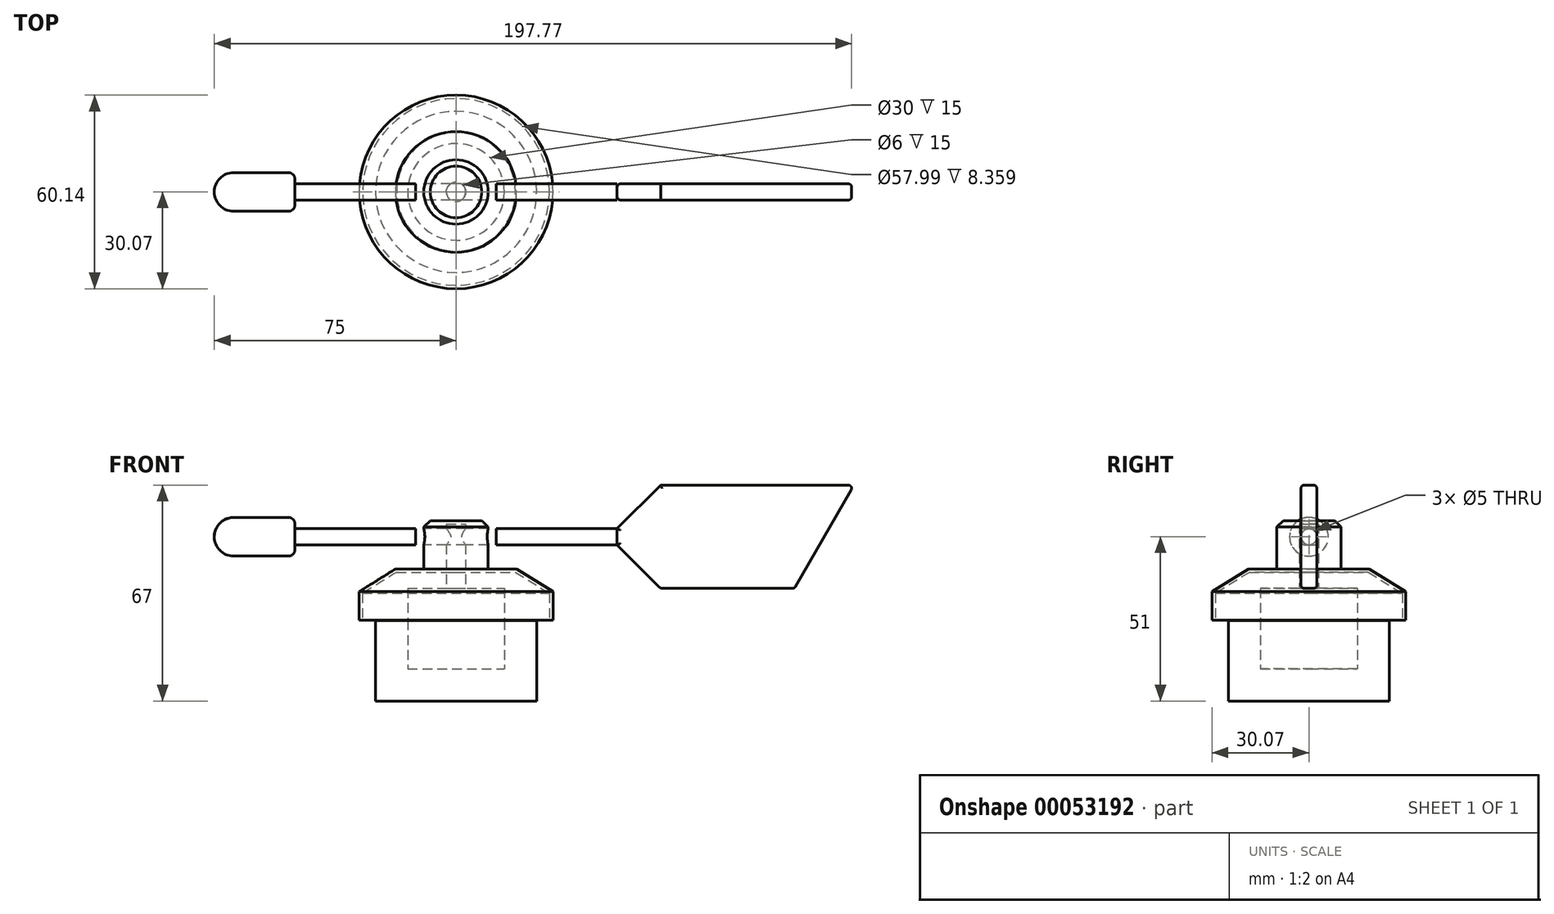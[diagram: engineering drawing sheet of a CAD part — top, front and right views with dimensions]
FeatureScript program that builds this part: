
annotation { "Feature Type Name" : "Feature", "Feature Type Description" : "" }
export const myFeature = defineFeature(function(context is Context, id is Id, definition is map)
    precondition{}
    {
        {
            var Q0;
            Q0=qCreatedBy(makeId("Front.planeOp"),FACE);
            var sketch = newSketch(context, id + "F0", { "sketchPlane" : qUnion([Q0])});
            skLineSegment(sketch, "E0", {"start": v(0, 0) * mm, "end": v(0, 20) * mm});
            skLineSegment(sketch, "E1", {"start": v(0, 20) * mm, "end": v(-3, 20) * mm});
            skLineSegment(sketch, "E2", {"start": v(-3, 20) * mm, "end": v(-3, 0) * mm});
            skLineSegment(sketch, "E3", {"start": v(-3, 0) * mm, "end": v(0, 0) * mm});
            skLineSegment(sketch, "E4", {"start": v(-3, 0) * mm, "end": v(-15, 0) * mm});
            skLineSegment(sketch, "E5", {"start": v(-15, 0) * mm, "end": v(-15, -25) * mm});
            skLineSegment(sketch, "E6", {"start": v(-15, -25) * mm, "end": v(0, -25) * mm});
            skLineSegment(sketch, "E7", {"start": v(0, -25) * mm, "end": v(0, 0) * mm});
            skLineSegment(sketch, "E8", {"start": v(-15, -10) * mm, "end": v(-25, -10) * mm});
            skLineSegment(sketch, "E9", {"start": v(-25, -10) * mm, "end": v(-25, -35) * mm});
            skLineSegment(sketch, "E10", {"start": v(-25, -35) * mm, "end": v(0, -35) * mm});
            skLineSegment(sketch, "E11", {"start": v(0, -35) * mm, "end": v(0, -25) * mm});
            skLineSegment(sketch, "E12", {"start": v(-10, 21) * mm, "end": v(-10, 6) * mm});
            skLineSegment(sketch, "E13", {"start": v(-10, 6) * mm, "end": v(-3, 6) * mm});
            skLineSegment(sketch, "E14", {"start": v(-10, 6) * mm, "end": v(-18.76, 6) * mm});
            skLineSegment(sketch, "E15", {"start": v(-18.76, 6) * mm, "end": v(-30.07, -1.04) * mm});
            skLineSegment(sketch, "E16", {"start": v(-30.07, -1.04) * mm, "end": v(-30.07, -9.93) * mm});
            skLineSegment(sketch, "E17", {"start": v(-30.07, -9.93) * mm, "end": v(-29, -9.93) * mm});
            skLineSegment(sketch, "E18", {"start": v(-29, -9.93) * mm, "end": v(-29, -1.58) * mm});
            skLineSegment(sketch, "E19", {"start": v(-29, -1.58) * mm, "end": v(-18.42, 5) * mm});
            skLineSegment(sketch, "E20", {"start": v(-18.42, 5) * mm, "end": v(-3, 5) * mm});
            skLineSegment(sketch, "E21", {"start": v(-10, 21) * mm, "end": v(0, 21) * mm});
            skLineSegment(sketch, "E22", {"start": v(0, 21) * mm, "end": v(0, 20) * mm});
            skSolve(sketch);
        }
        {
            var Q0;
            {var subQ2=sQuery(id+"F0.wireOp",EDGE,"E1");Q0=makeQuery(id+"F0.imprint","IMPRINT",FACE,{"disambiguationData":[TD([[makeQuery(id+"F0.imprint","IMPRINT",EDGE,{"derivedFrom":subQ2}),1.0]])]});}
            var Q1;
            Q1=sQuery(id+"F0.wireOp",EDGE,"E0");
            revolve(context, id + "F1", {"entities" : qUnion([Q0]), "axis" : qUnion([Q1]), "revolveType" : RevolveType.FULL});
        }
        {
            var Q0;
            Q0=makeQuery(id+"F0.imprint","IMPRINT",FACE,{"disambiguationData":[TD([[makeQuery(id+"F0.imprint","IMPRINT",EDGE,{"derivedFrom":sQuery(id+"F0.wireOp",EDGE,"E3")}),-1.0]])]});
            var Q1;
            Q1=sQuery(id+"F0.wireOp",EDGE,"E0");
            revolve(context, id + "F2", {"operationType" : NewBodyOperationType.ADD, "entities" : qUnion([Q0]), "axis" : qUnion([Q1]), "revolveType" : RevolveType.FULL});
        }
        {
            var Q0;
            {var subQ1=sQuery(id+"F0.wireOp",EDGE,"E6");Q0=makeQuery(id+"F0.imprint","IMPRINT",FACE,{"disambiguationData":[TD([[makeQuery(id+"F0.imprint","IMPRINT",EDGE,{"derivedFrom":subQ1}),-1.0]])]});}
            var Q1;
            Q1=sQuery(id+"F0.wireOp",EDGE,"E0");
            revolve(context, id + "F3", {"entities" : qUnion([Q0]), "axis" : qUnion([Q1]), "revolveType" : RevolveType.FULL});
        }
        {
            var Q0;
            {var subQ2=sQuery(id+"F0.wireOp",EDGE,"E1");Q0=makeQuery(id+"F0.imprint","IMPRINT",FACE,{"disambiguationData":[TD([[makeQuery(id+"F0.imprint","IMPRINT",EDGE,{"derivedFrom":subQ2}),-1.0]])]});}
            var Q1;
            {var subQ0=sQuery(id+"F0.wireOp",EDGE,"E13");Q1=makeQuery(id+"F0.imprint","IMPRINT",FACE,{"disambiguationData":[TD([[makeQuery(id+"F0.imprint","IMPRINT",EDGE,{"derivedFrom":subQ0}),-1.0]])]});}
            var Q2;
            Q2=sQuery(id+"F0.wireOp",EDGE,"E0");
            revolve(context, id + "F4", {"entities" : qUnion([Q0, Q1]), "axis" : qUnion([Q2]), "revolveType" : RevolveType.FULL});
        }
        {
            var Q0;
            Q0=qCreatedBy(makeId("Right.planeOp"),FACE);
            var sketch = newSketch(context, id + "F5", { "sketchPlane" : qUnion([Q0])});
            skCircle(sketch, "E23", {"center": v(0, 16) * mm, "radius": 2.5 * mm});
            skSolve(sketch);
        }
        {
            var Q0;
            Q0 = qSketchRegion(id + "F5", true);
            extrude(context, id + "F6", {"entities" : qUnion([Q0]), "endBound" : BoundingType.SYMMETRIC, "depth" : 100 * mm});
        }
        {
            var Q0;
            Q0=makeQuery(id+"F6.opExtrude","CAP_FACE",FACE,{"disambiguationData":[OSD([sQuery(id+"F5.wireOp",EDGE,"E23")])],"isStart":true});
            cPlane(context, id + "F7", {"entities" : qUnion([Q0]), "cplaneType" : CPlaneType.OFFSET, "offset" : 0 * mm, "width" : 150 * mm, "height" : 150 * mm});
        }
        {
            var Q0;
            Q0=qCreatedBy(id+"F7.planeOp",FACE);
            var sketch = newSketch(context, id + "F8", { "sketchPlane" : qUnion([Q0])});
            skCircle(sketch, "E24.0", {"center": v(0, 16) * mm, "radius": 2.5 * mm, "construction": true});
            skCircle(sketch, "E25", {"center": v(0, 16) * mm, "radius": 6 * mm});
            skSolve(sketch);
        }
        {
            var Q0;
            Q0=makeQuery(id+"F8.imprint","IMPRINT",FACE,{"disambiguationData":[TD([[makeQuery(id+"F8.imprint","IMPRINT",EDGE,{"derivedFrom":sQuery(id+"F8.wireOp",EDGE,"E25")}),1.0]])]});
            extrude(context, id + "F9", {"entities" : qUnion([Q0]), "depth" : 25 * mm});
        }
        {
            var Q0;
            Q0=makeQuery(id+"F9.opExtrude","CAP_EDGE",EDGE,{"disambiguationData":[OSD([sQuery(id+"F8.wireOp",EDGE,"E25")])],"isStart":false});
            fillet(context, id + "F10", {"entities" : qUnion([Q0]), "radius" : 6 * mm, "tangentPropagation" : true, "allowEdgeOverflow" : false});
        }
        {
            var Q0;
            Q0=makeQuery(id+"F9.opExtrude","CAP_EDGE",EDGE,{"disambiguationData":[OSD([sQuery(id+"F8.wireOp",EDGE,"E25")])],"isStart":true});
            fillet(context, id + "F11", {"entities" : qUnion([Q0]), "radius" : 2 * mm, "tangentPropagation" : true, "allowEdgeOverflow" : false});
        }
        {
            var Q0;
            Q0=qCreatedBy(makeId("Front.planeOp"),FACE);
            var sketch = newSketch(context, id + "F12", { "sketchPlane" : qUnion([Q0])});
            skLineSegment(sketch, "E26.0", {"start": v(50, 18.5) * mm, "end": v(50, 13.5) * mm, "construction": true});
            skLineSegment(sketch, "E27", {"start": v(50, 18.5) * mm, "end": v(63.5, 32) * mm});
            skLineSegment(sketch, "E28", {"start": v(63.5, 32) * mm, "end": v(123.5, 32) * mm});
            skLineSegment(sketch, "E29", {"start": v(123.5, 32) * mm, "end": v(105.02, 0) * mm});
            skLineSegment(sketch, "E30", {"start": v(105.02, 0) * mm, "end": v(63.5, 0) * mm});
            skLineSegment(sketch, "E31", {"start": v(63.5, 0) * mm, "end": v(50, 13.5) * mm});
            skLineSegment(sketch, "E32", {"start": v(50, 13.5) * mm, "end": v(50, 18.5) * mm});
            skSolve(sketch);
        }
        {
            var Q0;
            Q0=makeQuery(id+"F12.imprint","IMPRINT",FACE,{"disambiguationData":[TD([[makeQuery(id+"F12.imprint","IMPRINT",EDGE,{"derivedFrom":sQuery(id+"F12.wireOp",EDGE,"E27")}),-1.0]])]});
            extrude(context, id + "F13", {"entities" : qUnion([Q0]), "endBound" : BoundingType.SYMMETRIC, "depth" : 5 * mm});
        }
        {
            var Q0;
            Q0=makeQuery(id+"F13.opExtrude","CAP_FACE",FACE,{"disambiguationData":[OSD([sQuery(id+"F12.wireOp",EDGE,"E27"),sQuery(id+"F12.wireOp",EDGE,"E28"),sQuery(id+"F12.wireOp",EDGE,"E29"),sQuery(id+"F12.wireOp",EDGE,"E30"),sQuery(id+"F12.wireOp",EDGE,"E31"),sQuery(id+"F12.wireOp",EDGE,"E32")])],"isStart":false});
            var Q1;
            Q1=makeQuery(id+"F13.opExtrude","CAP_FACE",FACE,{"disambiguationData":[OSD([sQuery(id+"F12.wireOp",EDGE,"E27"),sQuery(id+"F12.wireOp",EDGE,"E28"),sQuery(id+"F12.wireOp",EDGE,"E29"),sQuery(id+"F12.wireOp",EDGE,"E30"),sQuery(id+"F12.wireOp",EDGE,"E31"),sQuery(id+"F12.wireOp",EDGE,"E32")])],"isStart":true});
            var Q2;
            Q2=makeQuery(id+"F13.opExtrude","SWEPT_EDGE",EDGE,{"disambiguationData":[OSD([sQuery(id+"F12.wireOp",EDGE,"E30"),sQuery(id+"F12.wireOp",EDGE,"E31")])]});
            var Q3;
            Q3=makeQuery(id+"F13.opExtrude","CAP_EDGE",EDGE,{"disambiguationData":[OSD([sQuery(id+"F12.wireOp",EDGE,"E27")])],"isStart":false});
            var Q4;
            Q4=makeQuery(id+"F13.opExtrude","SWEPT_EDGE",EDGE,{"disambiguationData":[OSD([sQuery(id+"F12.wireOp",EDGE,"E28"),sQuery(id+"F12.wireOp",EDGE,"E29")])]});
            var Q5;
            Q5=makeQuery(id+"F13.opExtrude","SWEPT_EDGE",EDGE,{"disambiguationData":[OSD([sQuery(id+"F12.wireOp",EDGE,"E29"),sQuery(id+"F12.wireOp",EDGE,"E30")])]});
            var Q6;
            Q6=makeQuery(id+"F13.opExtrude","CAP_EDGE",EDGE,{"disambiguationData":[OSD([sQuery(id+"F12.wireOp",EDGE,"E32")])],"isStart":false});
            var Q7;
            Q7=makeQuery(id+"F13.opExtrude","CAP_EDGE",EDGE,{"disambiguationData":[OSD([sQuery(id+"F12.wireOp",EDGE,"E32")])],"isStart":true});
            fillet(context, id + "F14", {"entities" : qUnion([Q0, Q1, Q2, Q3, Q4, Q5, Q6, Q7]), "radius" : 1 * mm, "tangentPropagation" : true, "allowEdgeOverflow" : false});
        }
        {
            var Q0;
            Q0=makeQuery(id+"F4.opRevolve","SWEPT_FACE",FACE,{"disambiguationData":[OSD([sQuery(id+"F0.wireOp",EDGE,"E21")])]});
            chamfer(context, id + "F15", {"entities" : qUnion([Q0]), "width" : 2 * mm, "tangentPropagation" : true});
        }
        {
            var Q0;
            Q0 = qSketchRegion(id + "F5", true);
            extrude(context, id + "F16", {"entities" : qUnion([Q0]), "operationType" : NewBodyOperationType.REMOVE, "endBound" : BoundingType.SYMMETRIC, "depth" : 25 * mm});
        }
    });
